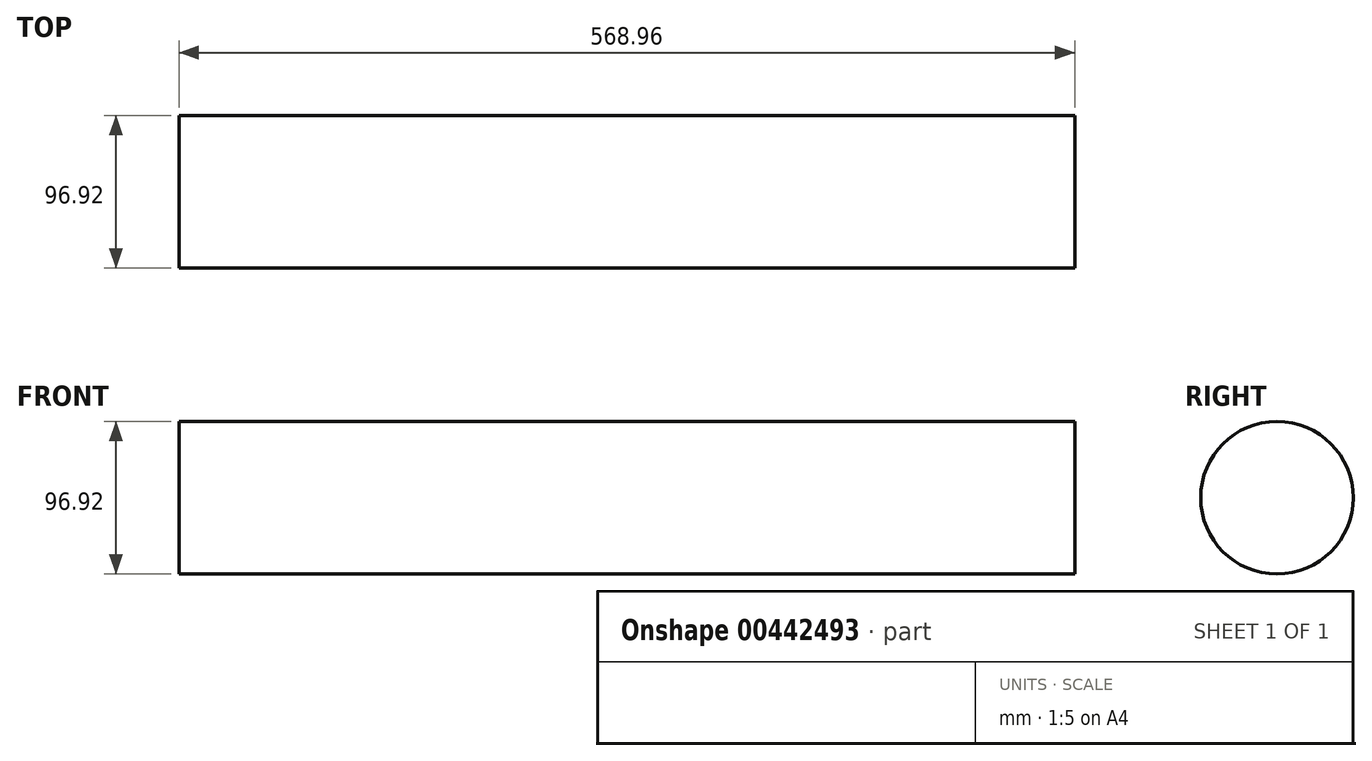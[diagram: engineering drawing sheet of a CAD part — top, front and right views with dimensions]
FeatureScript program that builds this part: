
annotation { "Feature Type Name" : "Feature", "Feature Type Description" : "" }
export const myFeature = defineFeature(function(context is Context, id is Id, definition is map)
    precondition{}
    {
        {
            var Q0;
            Q0=qCreatedBy(makeId("Right.planeOp"),FACE);
            var sketch = newSketch(context, id + "F0", { "sketchPlane" : qUnion([Q0])});
            skCircle(sketch, "E0", {"center": v(0, 0) * mm, "radius": 48.46 * mm});
            skSolve(sketch);
        }
        {
            var Q0;
            Q0=makeQuery(id+"F0.imprint","IMPRINT",FACE,{"disambiguationData":[TD([[makeQuery(id+"F0.imprint","IMPRINT",EDGE,{"derivedFrom":sQuery(id+"F0.wireOp",EDGE,"E0")}),1.0]])]});
            extrude(context, id + "F1", {"entities" : qUnion([Q0]), "endBound" : BoundingType.SYMMETRIC, "depth" : 568.96 * mm});
        }
    });
